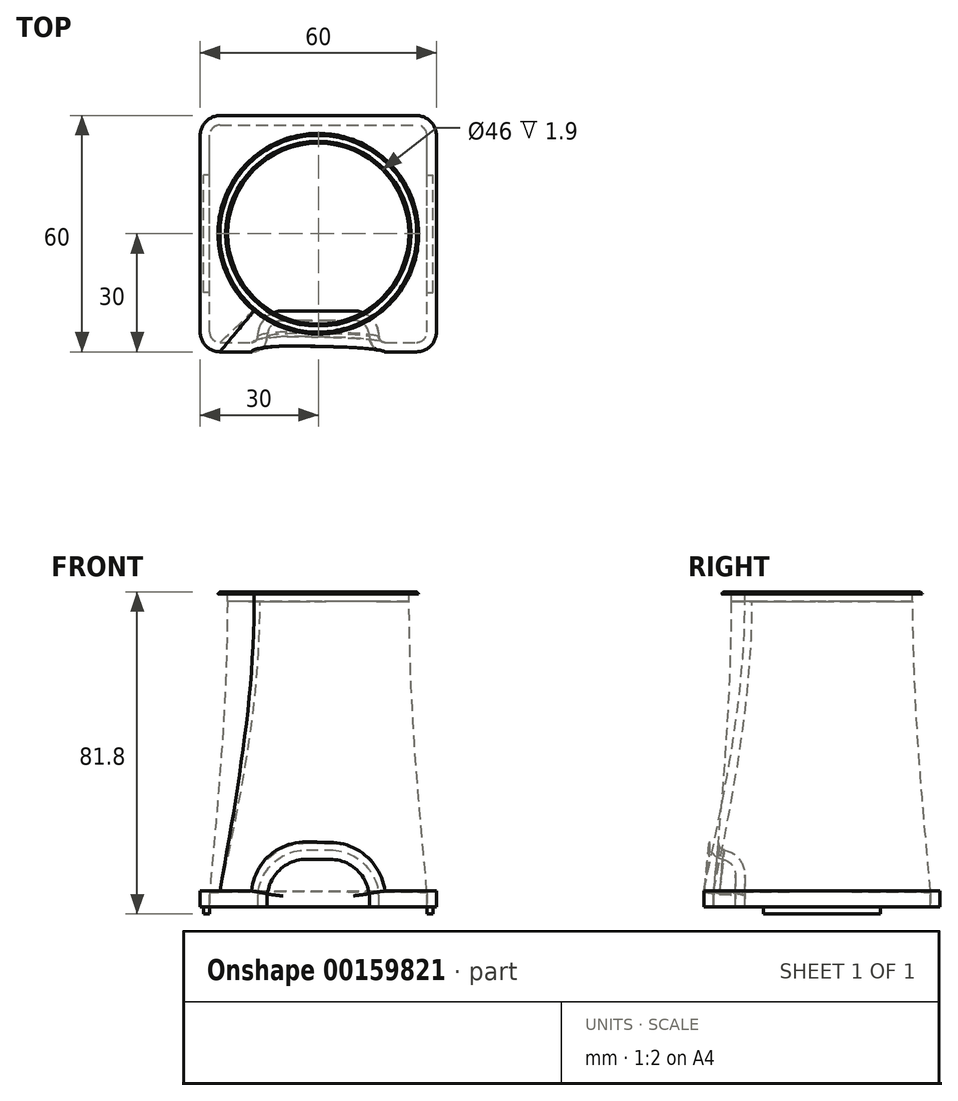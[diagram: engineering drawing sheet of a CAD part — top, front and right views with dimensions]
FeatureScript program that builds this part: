
annotation { "Feature Type Name" : "Feature", "Feature Type Description" : "" }
export const myFeature = defineFeature(function(context is Context, id is Id, definition is map)
    precondition{}
    {
        {
            var Q0;
            Q0=qCreatedBy(makeId("Top.planeOp"),FACE);
            var sketch = newSketch(context, id + "F0", { "sketchPlane" : qUnion([Q0])});
            skLineSegment(sketch, "E0.bottom", {"start": v(-25, 0) * mm, "end": v(25, 0) * mm});
            skLineSegment(sketch, "E0.top", {"start": v(-25, 60) * mm, "end": v(25, 60) * mm});
            skLineSegment(sketch, "E0.left", {"start": v(-30, 5) * mm, "end": v(-30, 55) * mm});
            skLineSegment(sketch, "E0.right", {"start": v(30, 5) * mm, "end": v(30, 55) * mm});
            skLineSegment(sketch, "E1", {"start": v(0, 0) * mm, "end": v(0, 60) * mm, "construction": true});
            skPoint(sketch, "E2.visualSharp", {"position": v(30, 60) * mm});
            skArc(sketch, "E2.filletArc", {"start": v(30, 55) * mm, "mid": v(28.54, 58.54) * mm, "end": v(25, 60) * mm});
            skPoint(sketch, "E3.visualSharp", {"position": v(-30, 60) * mm});
            skArc(sketch, "E3.filletArc", {"start": v(-25, 60) * mm, "mid": v(-28.54, 58.54) * mm, "end": v(-30, 55) * mm});
            skPoint(sketch, "E4.visualSharp", {"position": v(-30, 0) * mm});
            skArc(sketch, "E4.filletArc", {"start": v(-30, 5) * mm, "mid": v(-28.54, 1.46) * mm, "end": v(-25, 0) * mm});
            skPoint(sketch, "E5.visualSharp", {"position": v(30, 0) * mm});
            skArc(sketch, "E5.filletArc", {"start": v(25, 0) * mm, "mid": v(28.54, 1.46) * mm, "end": v(30, 5) * mm});
            skSolve(sketch);
        }
        {
            var Q0;
            Q0=makeQuery(id+"F0.imprint","IMPRINT",FACE,{"disambiguationData":[TD([[makeQuery(id+"F0.imprint","IMPRINT",EDGE,{"derivedFrom":sQuery(id+"F0.wireOp",EDGE,"E0.bottom")}),1.0]])]});
            extrude(context, id + "F1", {"entities" : qUnion([Q0]), "oppositeDirection" : true, "depth" : 4 * mm});
        }
        {
            var Q0;
            Q0=makeQuery(id+"F0.imprint","IMPRINT",FACE,{"disambiguationData":[TD([[makeQuery(id+"F0.imprint","IMPRINT",EDGE,{"derivedFrom":sQuery(id+"F0.wireOp",EDGE,"E0.bottom")}),1.0]])]});
            cPlane(context, id + "F2", {"entities" : qUnion([Q0]), "cplaneType" : CPlaneType.OFFSET, "offset" : 76 * mm, "width" : 150 * mm, "height" : 150 * mm});
        }
        {
            var Q0;
            Q0=qCreatedBy(id+"F2.planeOp",FACE);
            var sketch = newSketch(context, id + "F3", { "sketchPlane" : qUnion([Q0])});
            skCircle(sketch, "E6", {"center": v(0, 30) * mm, "radius": 25.5 * mm});
            skLineSegment(sketch, "E7", {"start": v(0, 30) * mm, "end": v(0, 4.5) * mm, "construction": true});
            skSolve(sketch);
        }
        {
            var Q0;
            Q0=makeQuery(id+"F3.imprint","IMPRINT",FACE,{"disambiguationData":[TD([[makeQuery(id+"F3.imprint","IMPRINT",EDGE,{"derivedFrom":sQuery(id+"F3.wireOp",EDGE,"E6")}),1.0]])]});
            cPlane(context, id + "F4", {"entities" : qUnion([Q0]), "cplaneType" : CPlaneType.OFFSET, "offset" : 4 * mm, "oppositeDirection" : true, "width" : 150 * mm, "height" : 150 * mm});
        }
        {
            var Q0;
            Q0=qCreatedBy(id+"F4.planeOp",FACE);
            var sketch = newSketch(context, id + "F5", { "sketchPlane" : qUnion([Q0])});
            skCircle(sketch, "E8", {"center": v(0, 30) * mm, "radius": 25.5 * mm});
            skSolve(sketch);
        }
        {
            var Q1;
            Q1=makeQuery(id+"F0.imprint","IMPRINT",FACE,{"disambiguationData":[TD([[makeQuery(id+"F0.imprint","IMPRINT",EDGE,{"derivedFrom":sQuery(id+"F0.wireOp",EDGE,"E0.bottom")}),1.0]])]});
            var Q2;
            Q2=makeQuery(id+"F5.imprint","IMPRINT",FACE,{"disambiguationData":[TD([[makeQuery(id+"F5.imprint","IMPRINT",EDGE,{"derivedFrom":sQuery(id+"F5.wireOp",EDGE,"E8")}),1.0]])]});
            var Q3;
            Q3=makeQuery(id+"F3.imprint","IMPRINT",FACE,{"disambiguationData":[TD([[makeQuery(id+"F3.imprint","IMPRINT",EDGE,{"derivedFrom":sQuery(id+"F3.wireOp",EDGE,"E6")}),1.0]])]});
            var Q4;
            {Q4=qUnion([sQuery(id+"F0.wireOp",EDGE,"E0.bottom"),sQuery(id+"F0.wireOp",EDGE,"E0.top"),sQuery(id+"F0.wireOp",EDGE,"E0.left"),sQuery(id+"F0.wireOp",EDGE,"E0.right"),sQuery(id+"F0.wireOp",EDGE,"E1"),sQuery(id+"F0.wireOp",EDGE,"E2.filletArc"),sQuery(id+"F0.wireOp",EDGE,"E3.filletArc"),sQuery(id+"F0.wireOp",EDGE,"E4.filletArc"),sQuery(id+"F0.wireOp",EDGE,"E5.filletArc")]);}
            loft(context, id + "F6", {"operationType" : NewBodyOperationType.ADD, "sheetProfilesArray" : [{ "sheetProfileEntities" : qUnion([Q1]) }, { "sheetProfileEntities" : qUnion([Q2]) }, { "sheetProfileEntities" : qUnion([Q3]) }], "guidesArray" : [{ "guideEntities" : qUnion([Q4]), "guideDerivativeType" : LoftGuideDerivativeType.DEFAULT, "guideDerivativeMagnitude" : 1 }]});
        }
        {
            var Q0;
            Q0=qCreatedBy(makeId("Front.planeOp"),FACE);
            var sketch = newSketch(context, id + "F7", { "sketchPlane" : qUnion([Q0])});
            skLineSegment(sketch, "E9.bottom", {"start": v(-13, -4) * mm, "end": v(13, -4) * mm});
            skLineSegment(sketch, "E9.top", {"start": v(-13, 8) * mm, "end": v(13, 8) * mm});
            skLineSegment(sketch, "E9.left", {"start": v(-13, -4) * mm, "end": v(-13, 8) * mm});
            skLineSegment(sketch, "E9.right", {"start": v(13, -4) * mm, "end": v(13, 8) * mm});
            skLineSegment(sketch, "E10", {"start": v(0, 8) * mm, "end": v(0, 0) * mm, "construction": true});
            skSolve(sketch);
        }
        {
            var Q0;
            Q0=makeQuery(id+"F7.imprint","IMPRINT",FACE,{"disambiguationData":[TD([[makeQuery(id+"F7.imprint","IMPRINT",EDGE,{"derivedFrom":sQuery(id+"F7.wireOp",EDGE,"E9.bottom")}),1.0]])]});
            extrude(context, id + "F8", {"entities" : qUnion([Q0]), "operationType" : NewBodyOperationType.REMOVE, "oppositeDirection" : true, "depth" : 8 * mm});
        }
        {
            var Q0;
            Q0=makeQuery(id+"F8.boolean.opBoolean","COPY",EDGE,{"derivedFrom":makeQuery(id+"F8.opExtrude","SWEPT_EDGE",EDGE,{"disambiguationData":[OSD([sQuery(id+"F7.wireOp",EDGE,"E9.top"),sQuery(id+"F7.wireOp",EDGE,"E9.left")])]})});
            var Q1;
            Q1=makeQuery(id+"F8.boolean.opBoolean","COPY",EDGE,{"derivedFrom":makeQuery(id+"F8.opExtrude","SWEPT_EDGE",EDGE,{"disambiguationData":[OSD([sQuery(id+"F7.wireOp",EDGE,"E9.top"),sQuery(id+"F7.wireOp",EDGE,"E9.right")])]})});
            fillet(context, id + "F9", {"entities" : qUnion([Q0, Q1]), "radius" : 10 * mm, "tangentPropagation" : true, "allowEdgeOverflow" : false});
        }
        {
            var Q0;
            Q0=makeQuery(id+"F9.opFillet","BLEND_EDGE",EDGE,{"blendedFrom":[makeQuery(id+"F8.boolean.opBoolean","COPY",EDGE,{"derivedFrom":makeQuery(id+"F8.opExtrude","SWEPT_EDGE",EDGE,{"disambiguationData":[OSD([sQuery(id+"F7.wireOp",EDGE,"E9.top"),sQuery(id+"F7.wireOp",EDGE,"E9.left")])]})}),makeQuery(id+"F6.opLoft","SWEPT_FACE",FACE,{"disambiguationData":[OSD([sQuery(id+"F0.wireOp",EDGE,"E0.bottom"),sQuery(id+"F0.wireOp",EDGE,"E4.filletArc"),sQuery(id+"F0.wireOp",EDGE,"E5.filletArc"),sQuery(id+"F5.wireOp",EDGE,"E8")])]})],"blendedInto":[makeQuery(id+"F6.opLoft","SWEPT_FACE",FACE,{"disambiguationData":[OSD([sQuery(id+"F0.wireOp",EDGE,"E0.bottom"),sQuery(id+"F0.wireOp",EDGE,"E4.filletArc"),sQuery(id+"F0.wireOp",EDGE,"E5.filletArc"),sQuery(id+"F5.wireOp",EDGE,"E8")])]})]});
            var Q1;
            {var subQ0=sQuery(id+"F7.wireOp",EDGE,"E9.left");var subQ1=sQuery(id+"F0.wireOp",EDGE,"E0.bottom");var subQ2=sQuery(id+"F0.wireOp",EDGE,"E4.filletArc");Q1=makeQuery(id+"F9.opFillet","BLEND_EDGE",EDGE,{"blendedFrom":[makeQuery(id+"F8.boolean.opBoolean","COPY",EDGE,{"derivedFrom":makeQuery(id+"F8.opExtrude","SWEPT_EDGE",EDGE,{"disambiguationData":[OSD([sQuery(id+"F7.wireOp",EDGE,"E9.top"),subQ0])]})}),makeQuery(id+"F8.boolean.opBoolean","SPLIT",FACE,{"disambiguationData":[TD([makeQuery(id+"F1.opExtrude","SWEPT_FACE",FACE,{"disambiguationData":[OSD([subQ2])]})])],"derivedFrom":makeQuery(id+"F1.opExtrude","SWEPT_FACE",FACE,{"disambiguationData":[OSD([subQ1])]})})],"blendedInto":[makeQuery(id+"F8.boolean.opBoolean","SPLIT",FACE,{"disambiguationData":[TD([makeQuery(id+"F1.opExtrude","SWEPT_FACE",FACE,{"disambiguationData":[OSD([subQ2])]})])],"derivedFrom":makeQuery(id+"F1.opExtrude","SWEPT_FACE",FACE,{"disambiguationData":[OSD([subQ1])]})})]});}
            var Q2;
            Q2=makeQuery(id+"F8.boolean.opBoolean","COPY",EDGE,{"derivedFrom":makeQuery(id+"F8.opExtrude","CAP_EDGE",EDGE,{"disambiguationData":[OSD([sQuery(id+"F7.wireOp",EDGE,"E9.left")])],"isStart":true})});
            var Q3;
            {var subQ0=sQuery(id+"F7.wireOp",EDGE,"E9.right");var subQ1=sQuery(id+"F0.wireOp",EDGE,"E0.bottom");var subQ3=sQuery(id+"F0.wireOp",EDGE,"E5.filletArc");Q3=makeQuery(id+"F9.opFillet","BLEND_EDGE",EDGE,{"blendedFrom":[makeQuery(id+"F8.boolean.opBoolean","COPY",EDGE,{"derivedFrom":makeQuery(id+"F8.opExtrude","SWEPT_EDGE",EDGE,{"disambiguationData":[OSD([sQuery(id+"F7.wireOp",EDGE,"E9.top"),subQ0])]})}),makeQuery(id+"F8.boolean.opBoolean","SPLIT",FACE,{"disambiguationData":[TD([makeQuery(id+"F1.opExtrude","SWEPT_FACE",FACE,{"disambiguationData":[OSD([subQ3])]})])],"derivedFrom":makeQuery(id+"F1.opExtrude","SWEPT_FACE",FACE,{"disambiguationData":[OSD([subQ1])]})})],"blendedInto":[makeQuery(id+"F8.boolean.opBoolean","SPLIT",FACE,{"disambiguationData":[TD([makeQuery(id+"F1.opExtrude","SWEPT_FACE",FACE,{"disambiguationData":[OSD([subQ3])]})])],"derivedFrom":makeQuery(id+"F1.opExtrude","SWEPT_FACE",FACE,{"disambiguationData":[OSD([subQ1])]})})]});}
            var Q4;
            Q4=makeQuery(id+"F8.boolean.opBoolean","COPY",EDGE,{"derivedFrom":makeQuery(id+"F8.opExtrude","CAP_EDGE",EDGE,{"disambiguationData":[OSD([sQuery(id+"F7.wireOp",EDGE,"E9.right")])],"isStart":true})});
            fillet(context, id + "F10", {"entities" : qUnion([Q0, Q1, Q2, Q3, Q4]), "radius" : 4 * mm, "tangentPropagation" : true, "allowEdgeOverflow" : false});
        }
        {
            var Q0;
            {var subQ0=sQuery(id+"F7.wireOp",EDGE,"E9.top");var subQ1=sQuery(id+"F7.wireOp",EDGE,"E9.left");Q0=makeQuery(id+"F9.opFillet","BLEND_EDGE",EDGE,{"blendedFrom":[makeQuery(id+"F8.boolean.opBoolean","COPY",EDGE,{"derivedFrom":makeQuery(id+"F8.opExtrude","SWEPT_EDGE",EDGE,{"disambiguationData":[OSD([subQ0,subQ1])]})}),makeQuery(id+"F8.boolean.opBoolean","COPY",FACE,{"derivedFrom":makeQuery(id+"F8.opExtrude","CAP_FACE",FACE,{"disambiguationData":[OSD([sQuery(id+"F7.wireOp",EDGE,"E9.bottom"),subQ0,subQ1,sQuery(id+"F7.wireOp",EDGE,"E9.right")])],"isStart":false})})],"blendedInto":[makeQuery(id+"F8.boolean.opBoolean","COPY",FACE,{"derivedFrom":makeQuery(id+"F8.opExtrude","CAP_FACE",FACE,{"disambiguationData":[OSD([sQuery(id+"F7.wireOp",EDGE,"E9.bottom"),subQ0,subQ1,sQuery(id+"F7.wireOp",EDGE,"E9.right")])],"isStart":false})})]});}
            fillet(context, id + "F11", {"entities" : qUnion([Q0]), "radius" : 4 * mm, "tangentPropagation" : true, "allowEdgeOverflow" : false});
        }
        {
            var Q0;
            Q0=makeQuery(id+"F1.opExtrude","CAP_FACE",FACE,{"disambiguationData":[OSD([sQuery(id+"F0.wireOp",EDGE,"E0.bottom"),sQuery(id+"F0.wireOp",EDGE,"E0.top"),sQuery(id+"F0.wireOp",EDGE,"E0.left"),sQuery(id+"F0.wireOp",EDGE,"E0.right"),sQuery(id+"F0.wireOp",EDGE,"E2.filletArc"),sQuery(id+"F0.wireOp",EDGE,"E3.filletArc"),sQuery(id+"F0.wireOp",EDGE,"E4.filletArc"),sQuery(id+"F0.wireOp",EDGE,"E5.filletArc")])],"isStart":false});
            shell(context, id + "F12", {"entities" : qUnion([Q0]), "thickness" : 2.4 * mm});
        }
        {
            var Q0;
            Q0=makeQuery(id+"F6.opLoft","CAP_FACE",FACE,{"disambiguationData":[OSD([makeQuery(id+"F3.imprint","IMPRINT",FACE,{"disambiguationData":[TD([[makeQuery(id+"F3.imprint","IMPRINT",EDGE,{"derivedFrom":sQuery(id+"F3.wireOp",EDGE,"E6")}),1.0]])]})])],"isStart":true});
            var sketch = newSketch(context, id + "F13", { "sketchPlane" : qUnion([Q0])});
            skCircle(sketch, "E11", {"center": v(0, 30) * mm, "radius": 25.5 * mm});
            skCircle(sketch, "E12.0", {"center": v(0, 30) * mm, "radius": 23 * mm});
            skSolve(sketch);
        }
        {
            var Q0;
            Q0=makeQuery(id+"F13.imprint","IMPRINT",FACE,{"disambiguationData":[TD([[makeQuery(id+"F13.imprint","IMPRINT",EDGE,{"derivedFrom":sQuery(id+"F13.wireOp",EDGE,"E12.0")}),1.0]])]});
            extrude(context, id + "F14", {"entities" : qUnion([Q0]), "operationType" : NewBodyOperationType.REMOVE, "oppositeDirection" : true, "depth" : 10 * mm});
        }
        {
            var Q0;
            Q0=makeQuery(id+"F1.opExtrude","CAP_FACE",FACE,{"disambiguationData":[OSD([sQuery(id+"F0.wireOp",EDGE,"E0.bottom"),sQuery(id+"F0.wireOp",EDGE,"E0.top"),sQuery(id+"F0.wireOp",EDGE,"E0.left"),sQuery(id+"F0.wireOp",EDGE,"E0.right"),sQuery(id+"F0.wireOp",EDGE,"E2.filletArc"),sQuery(id+"F0.wireOp",EDGE,"E3.filletArc"),sQuery(id+"F0.wireOp",EDGE,"E4.filletArc"),sQuery(id+"F0.wireOp",EDGE,"E5.filletArc")])],"isStart":false});
            var sketch = newSketch(context, id + "F15", { "sketchPlane" : qUnion([Q0])});
            skLineSegment(sketch, "E13.bottom", {"start": v(-27.6, -15.1) * mm, "end": v(-29.2, -15.1) * mm});
            skLineSegment(sketch, "E13.top", {"start": v(-27.6, -44.9) * mm, "end": v(-29.2, -44.9) * mm});
            skLineSegment(sketch, "E13.left", {"start": v(-27.6, -15.1) * mm, "end": v(-27.6, -44.9) * mm});
            skLineSegment(sketch, "E13.right", {"start": v(-29.2, -15.1) * mm, "end": v(-29.2, -44.9) * mm});
            skLineSegment(sketch, "E14.bottom", {"start": v(27.6, -15.1) * mm, "end": v(29.2, -15.1) * mm});
            skLineSegment(sketch, "E14.top", {"start": v(27.6, -44.9) * mm, "end": v(29.2, -44.9) * mm});
            skLineSegment(sketch, "E14.left", {"start": v(27.6, -15.1) * mm, "end": v(27.6, -44.9) * mm});
            skLineSegment(sketch, "E14.right", {"start": v(29.2, -15.1) * mm, "end": v(29.2, -44.9) * mm});
            skLineSegment(sketch, "E15", {"start": v(29.2, -30) * mm, "end": v(30, -30) * mm, "construction": true});
            skSolve(sketch);
        }
        {
            var Q0;
            {Q0=qUnion([makeQuery(id+"F15.imprint","IMPRINT",FACE,{"disambiguationData":[TD([[makeQuery(id+"F15.imprint","IMPRINT",EDGE,{"derivedFrom":sQuery(id+"F15.wireOp",EDGE,"E13.bottom")}),1.0]])]}),makeQuery(id+"F15.imprint","IMPRINT",FACE,{"disambiguationData":[TD([[makeQuery(id+"F15.imprint","IMPRINT",EDGE,{"derivedFrom":sQuery(id+"F15.wireOp",EDGE,"E14.bottom")}),-1.0]])]})]);}
            extrude(context, id + "F16", {"entities" : qUnion([Q0]), "operationType" : NewBodyOperationType.ADD, "depth" : 1.8 * mm});
        }
        {
            var Q0;
            Q0=makeQuery(id+"F6.opLoft","CAP_FACE",FACE,{"disambiguationData":[OSD([makeQuery(id+"F3.imprint","IMPRINT",FACE,{"disambiguationData":[TD([[makeQuery(id+"F3.imprint","IMPRINT",EDGE,{"derivedFrom":sQuery(id+"F3.wireOp",EDGE,"E6")}),1.0]])]})])],"isStart":true});
            chamfer(context, id + "F17", {"entities" : qUnion([Q0]), "width" : .5 * mm, "tangentPropagation" : true});
        }
    });
